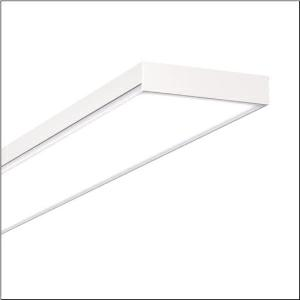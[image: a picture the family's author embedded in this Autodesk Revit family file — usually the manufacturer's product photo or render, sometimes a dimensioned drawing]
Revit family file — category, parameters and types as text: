
# Revit family: apollon_r__31_surface_51mp26wd2341w_2791
name_source: partatom
category: Lighting Fixtures
units: mm (PartAtom-declared; Revit-internal decimal feet)

## family parameters
Cut with Voids When Loaded = No
Host = Face
Light Source = No
Part Type = Normal
Room Calculation Point = No
Round Connector Dimension = Use Diameter
Shared = No

## types (1)
- Apollon® 31 Surface (1 x LED, 4400 lm, 33 W, 3000K)
    Apparent Load = 33 VA
    CIE Flux Codes = 61 87 97 97 100
    Color Rendering = 80
    Color Temperature = 3000K
    Default Elevation = 1800 mm
    Description = Apollon® 31 Surface, office luminaire, primary optical cover: micro prismatic cover, of PMMA, light emission: direct distribution, primary light characteristic: symmetric, installation type: surface-mounted, LED, rated luminous flux: 4.400lm, luminous efficacy: 133lm/W, light colour: 830, colour temperature: 3000K, control gear: ECG DALI, with terminal, 5-pole, mains connection: 220..240V, AC, 50/60Hz, rated input power: 33W, housing, of sheet steel, coil coated, traffic white (RAL 9016), length: 1.545mm, width: 200mm, height: 44mm, protection rating (complete): IP20, insulation class (complete): insulation class II (safety insulation), certification: CE, impact resistance: IK02, permissible operating ambient temperature: -20..+40°C, standard: EN 60598-2-22, packaging unit: 1 piece
    Height = 44 mm
    Lamp = 1 x LED
    Lamp Light Flux = 4400 lm
    Lamp Power = 33 W
    Lamp count = 1
    Length = 1545 mm
    Luminous efficacy = 133 lm/W
    Manufacturer = Siteco
    ModVariant = No
    Model = 51MP26WD2341W
    Mounting Place = Ceiling
    Mounting Type = Surface mounted
    Number of Poles = 1
    OnlyDefault = Yes
    Power Factor = 1
    Product Name = Apollon® 31 Surface
    Product group = office luminaire | ceiling mounted
    ProductGroupID = 304
    Protection Class = Protection class II
    Protection Degree = IP 20
    RLX_Detail_Level = 1
    RLX_Emergency_Light_Flux = 0 lm
    RLX_Emergency_Type = 0
    RLX_Emergency_Type_DB = No
    RlxData = <blob elided: 20757 chars, md5=c760fe8b>
    Socket = socket
    Standby Power = 0 W
    System Light Flux = 4400 lm
    System Power = 33 W
    Type Comments = Product without accessories
    Type Image = l_1007095.jpg
    URL = http://relux.com
    VarID = ---
    Voltage = 0 V
    Weight = 0.00 kg
    Width = 200 mm  [stored 0.656168 ft]

note: [stored X ft] marks values corroborated as IEEE doubles in the binary element streams (Revit-internal decimal feet)

## geometry (parser evidence)
native form markers: Blend x4, Sweep x11
no freeform markers — native parametric forms only
